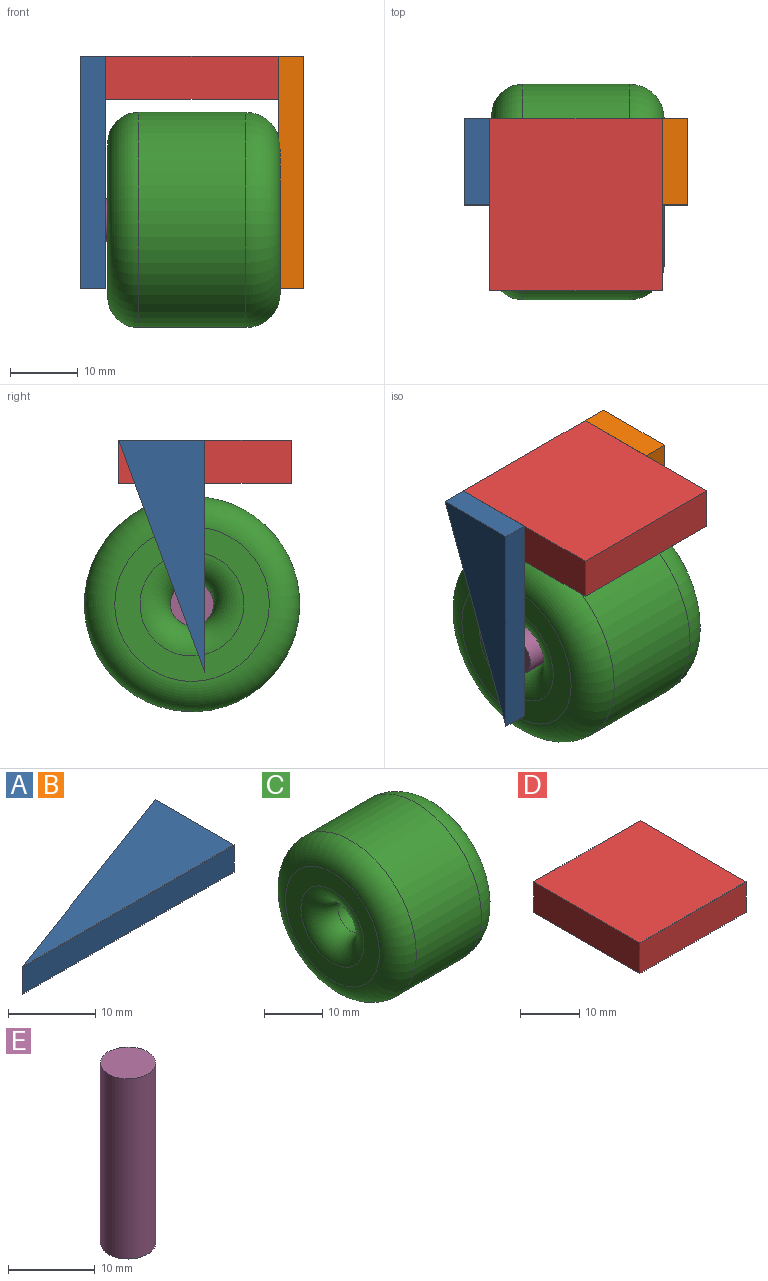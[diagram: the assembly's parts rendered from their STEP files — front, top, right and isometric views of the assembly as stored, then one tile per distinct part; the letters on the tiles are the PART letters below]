
ASSEMBLY  parts=5 mates=4
PART A: 5 faces, bbox 34.3x12.7x3.8 mm
  f0: plane 34.29x12.7mm, normal (-0.35,0.94,0), area 139.3mm2, adj f1,f2,f3,f4
  f1: plane 34.29x3.81mm, normal (0,-1,0), area 130.6mm2, adj f0,f2,f3,f4
  f2: plane 12.7x3.81mm, normal (1,0,0), area 48.4mm2, adj f0,f1,f3,f4
  f3: plane 34.29x12.7mm, normal (0,0,1), area 217.7mm2, adj f0,f1,f2
  f4: plane 34.29x12.7mm, normal (0,0,-1), area 217.7mm2, adj f0,f1,f2
PART B: same geometry as A
PART C: 8 faces, bbox 25.4x34.4x34.4 mm
  f0: cylinder r=3.17mm len=15.83mm, axis (-1,0,0), area 315.8mm2, adj f4,f6
  f1: cylinder r=15.88mm len=31.75mm, axis (-1,0,0), area 1579.2mm2, adj f5,f7
  f2: plane 21.59x21.59mm, normal (1,0,0), area 152mm2, adj f4,f5
  f3: plane 22.78x22.78mm, normal (-1,0,0), area 222.9mm2, adj f6,f7
  f4: torus R=8.26mm, axis (1,0,0), area 251.7mm2, adj f0,f2
  f5: torus R=10.79mm, axis (1,0,0), area 703.4mm2, adj f1,f2
  f6: torus R=7.66mm, axis (1,0,0), area 212.8mm2, adj f0,f3
  f7: torus R=11.39mm, axis (1,0,0), area 630.9mm2, adj f1,f3
PART D: 6 faces, bbox 25.4x25.4x6.4 mm
  f0: plane 25.4x6.35mm, normal (-1,0,0), area 161.3mm2, adj f1,f3,f4,f5
  f1: plane 25.4x6.35mm, normal (0,-1,0), area 161.3mm2, adj f0,f2,f4,f5
  f2: plane 25.4x6.35mm, normal (1,0,0), area 161.3mm2, adj f1,f3,f4,f5
  f3: plane 25.4x6.35mm, normal (0,1,0), area 161.3mm2, adj f0,f2,f4,f5
  f4: plane 25.4x25.4mm, normal (0,0,1), area 645.2mm2, adj f0,f1,f2,f3
  f5: plane 25.4x25.4mm, normal (0,0,-1), area 645.2mm2, adj f0,f1,f2,f3
PART E: 3 faces, bbox 6.4x6.4x25.4 mm
  f0: cylinder r=3.17mm len=25.4mm, axis (0,0,-1), area 506.7mm2, adj f1,f2
  f1: plane 6.35x6.35mm, normal (0,0,1), area 31.7mm2, adj f0
  f2: plane 6.35x6.35mm, normal (0,0,-1), area 31.7mm2, adj f0
PLACE A rot(axis=(0,-1,0),90deg) t=(-51.16,-62.56,-30.21)mm
PLACE B rot(axis=(0,-1,0),90deg) t=(-21.95,-62.56,-30.21)mm
PLACE C rot(axis=(1,0,0),152.1deg) t=(-50.86,-13.56,-3.61)mm
PLACE D t=(0,-47.12,14.17)mm
PLACE E rot(axis=(-0.58,0.58,-0.58),120deg) t=(-51.16,-67.57,-26.34)mm
MATE revolute E.f0 <-> C.f0  axis (-1,0,0) through (-38.46,-13.56,-3.61)mm
MATE fastened A.f4 <-> D.f0  axis (1,0,0) through (-51.16,-15.46,20.52)mm
MATE fastened E.f0 <-> B.f3  axis (1,0,0) through (-25.76,-13.56,-3.61)mm
MATE fastened B.f3 <-> D.f2  axis (-1,0,0) through (-25.76,-15.46,20.52)mm
